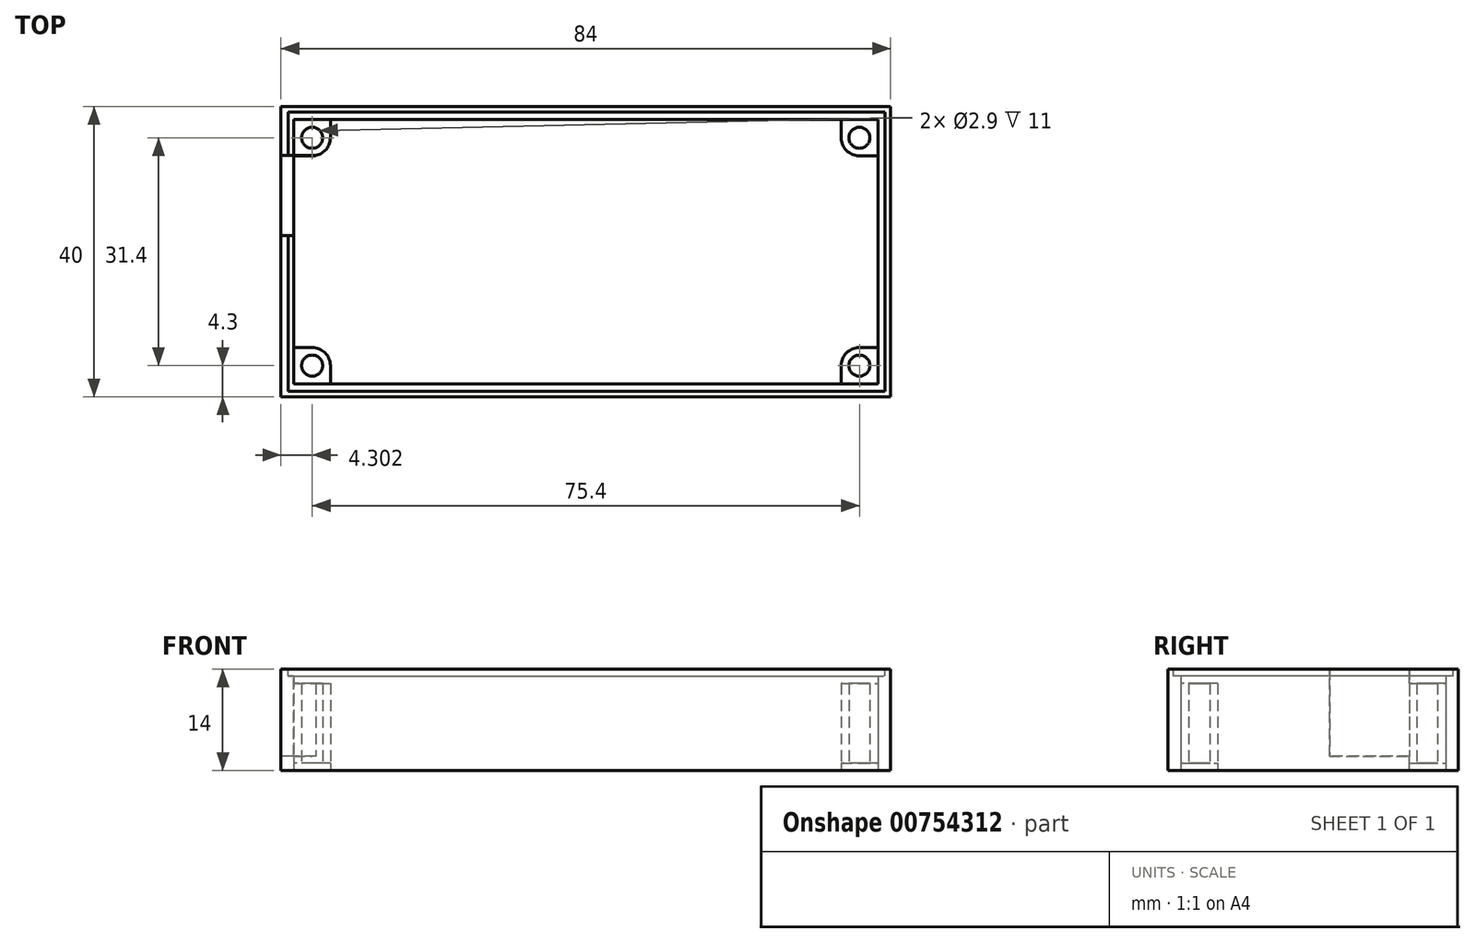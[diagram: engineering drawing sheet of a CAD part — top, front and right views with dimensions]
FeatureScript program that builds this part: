
annotation { "Feature Type Name" : "Feature", "Feature Type Description" : "" }
export const myFeature = defineFeature(function(context is Context, id is Id, definition is map)
    precondition{}
    {
        {
            var Q0;
            Q0=qCreatedBy(makeId("Top.planeOp"),FACE);
            var sketch = newSketch(context, id + "F0", { "sketchPlane" : qUnion([Q0])});
            skLineSegment(sketch, "E0.bottom", {"start": v(-40.69, 13.07) * mm, "end": v(39.81, 13.07) * mm});
            skLineSegment(sketch, "E0.top", {"start": v(-40.69, -23.43) * mm, "end": v(39.81, -23.43) * mm});
            skLineSegment(sketch, "E0.left", {"start": v(-40.69, 13.07) * mm, "end": v(-40.69, -23.43) * mm});
            skLineSegment(sketch, "E0.right", {"start": v(39.81, 13.07) * mm, "end": v(39.81, -23.43) * mm});
            skCircle(sketch, "E1", {"center": v(-38.14, 10.52) * mm, "radius": 1.45 * mm});
            skLineSegment(sketch, "E2", {"start": v(-0.44, 13.07) * mm, "end": v(-0.44, -23.43) * mm, "construction": true});
            skLineSegment(sketch, "E3", {"start": v(-40.69, -5.18) * mm, "end": v(39.81, -5.18) * mm, "construction": true});
            skLineSegment(sketch, "E4.bottom", {"start": v(-42.44, 14.82) * mm, "end": v(41.56, 14.82) * mm});
            skLineSegment(sketch, "E4.top", {"start": v(-42.44, -25.18) * mm, "end": v(41.56, -25.18) * mm});
            skLineSegment(sketch, "E4.left", {"start": v(-42.44, 14.82) * mm, "end": v(-42.44, -25.18) * mm});
            skLineSegment(sketch, "E4.right", {"start": v(41.56, 14.82) * mm, "end": v(41.56, -25.18) * mm});
            skArc(sketch, "E5", {"start": v(-35.64, 10.52) * mm, "mid": v(-36.37, 8.75) * mm, "end": v(-38.14, 8.02) * mm});
            skLineSegment(sketch, "E6", {"start": v(-35.64, 10.52) * mm, "end": v(-35.64, 13.07) * mm});
            skLineSegment(sketch, "E7", {"start": v(-38.14, 8.02) * mm, "end": v(-40.69, 8.02) * mm});
            skCircle(sketch, "E8.MirrorC", {"center": v(37.26, 10.52) * mm, "radius": 1.45 * mm});
            skLineSegment(sketch, "E9.MirrorCS", {"start": v(34.76, 10.52) * mm, "end": v(34.76, 13.07) * mm});
            skLineSegment(sketch, "E10.MirrorCS", {"start": v(37.26, 8.02) * mm, "end": v(39.81, 8.02) * mm});
            skArc(sketch, "E11.MirrorCS", {"start": v(34.76, 10.52) * mm, "mid": v(35.5, 8.75) * mm, "end": v(37.26, 8.02) * mm});
            skCircle(sketch, "E12.MirrorC", {"center": v(37.26, -20.88) * mm, "radius": 1.45 * mm});
            skLineSegment(sketch, "E13.MirrorCS", {"start": v(37.26, -18.38) * mm, "end": v(39.81, -18.38) * mm});
            skArc(sketch, "E14.MirrorCS", {"start": v(34.76, -20.88) * mm, "mid": v(35.5, -19.11) * mm, "end": v(37.26, -18.38) * mm});
            skLineSegment(sketch, "E15.MirrorCS", {"start": v(34.76, -20.88) * mm, "end": v(34.76, -23.43) * mm});
            skCircle(sketch, "E16.MirrorC", {"center": v(-38.14, -20.88) * mm, "radius": 1.45 * mm});
            skLineSegment(sketch, "E17.MirrorCS", {"start": v(-35.64, -20.88) * mm, "end": v(-35.64, -23.43) * mm});
            skLineSegment(sketch, "E18.MirrorCS", {"start": v(-38.14, -18.38) * mm, "end": v(-40.69, -18.38) * mm});
            skArc(sketch, "E19.MirrorCS", {"start": v(-35.64, -20.88) * mm, "mid": v(-36.37, -19.11) * mm, "end": v(-38.14, -18.38) * mm});
            skPoint(sketch, "E20.0.midPoint", {"position": v(39.73, 9.1) * mm});
            skPoint(sketch, "E21.0.midPoint", {"position": v(39.73, -22.3) * mm});
            skPoint(sketch, "E22.0.midPoint", {"position": v(-35.67, -22.3) * mm});
            skPoint(sketch, "E23.0.midPoint", {"position": v(-35.67, 9.1) * mm});
            skSolve(sketch);
        }
        {
            var Q0;
            Q0=makeQuery(id+"F0.imprint","IMPRINT",FACE,{"disambiguationData":[TD([[makeQuery(id+"F0.imprint","IMPRINT",EDGE,{"derivedFrom":sQuery(id+"F0.wireOp",EDGE,"E8.MirrorC")}),-1.0]])]});
            var Q1;
            Q1=makeQuery(id+"F0.imprint","IMPRINT",FACE,{"disambiguationData":[TD([[makeQuery(id+"F0.imprint","IMPRINT",EDGE,{"derivedFrom":sQuery(id+"F0.wireOp",EDGE,"E5")}),1.0]])]});
            var Q2;
            Q2=makeQuery(id+"F0.imprint","IMPRINT",FACE,{"disambiguationData":[TD([[makeQuery(id+"F0.imprint","IMPRINT",EDGE,{"derivedFrom":sQuery(id+"F0.wireOp",EDGE,"E4.bottom")}),-1.0]])]});
            var Q3;
            Q3=makeQuery(id+"F0.imprint","IMPRINT",FACE,{"disambiguationData":[TD([[makeQuery(id+"F0.imprint","IMPRINT",EDGE,{"derivedFrom":sQuery(id+"F0.wireOp",EDGE,"E12.MirrorC")}),-1.0]])]});
            var Q4;
            Q4=makeQuery(id+"F0.imprint","IMPRINT",FACE,{"disambiguationData":[TD([[makeQuery(id+"F0.imprint","IMPRINT",EDGE,{"derivedFrom":sQuery(id+"F0.wireOp",EDGE,"E8.MirrorC")}),1.0]])]});
            var Q5;
            Q5=makeQuery(id+"F0.imprint","IMPRINT",FACE,{"disambiguationData":[TD([[makeQuery(id+"F0.imprint","IMPRINT",EDGE,{"derivedFrom":sQuery(id+"F0.wireOp",EDGE,"E1")}),1.0]])]});
            var Q6;
            Q6=makeQuery(id+"F0.imprint","IMPRINT",FACE,{"disambiguationData":[TD([[makeQuery(id+"F0.imprint","IMPRINT",EDGE,{"derivedFrom":sQuery(id+"F0.wireOp",EDGE,"E12.MirrorC")}),1.0]])]});
            var Q7;
            Q7=makeQuery(id+"F0.imprint","IMPRINT",FACE,{"disambiguationData":[TD([[makeQuery(id+"F0.imprint","IMPRINT",EDGE,{"derivedFrom":sQuery(id+"F0.wireOp",EDGE,"E16.MirrorC")}),-1.0]])]});
            var Q8;
            Q8=makeQuery(id+"F0.imprint","IMPRINT",FACE,{"disambiguationData":[TD([[makeQuery(id+"F0.imprint","IMPRINT",EDGE,{"derivedFrom":sQuery(id+"F0.wireOp",EDGE,"E16.MirrorC")}),1.0]])]});
            var Q9;
            Q9=makeQuery(id+"F0.imprint","IMPRINT",FACE,{"disambiguationData":[TD([[makeQuery(id+"F0.imprint","IMPRINT",EDGE,{"derivedFrom":sQuery(id+"F0.wireOp",EDGE,"E1")}),-1.0]])]});
            extrude(context, id + "F1", {"entities" : qUnion([Q0, Q1, Q2, Q3, Q4, Q5, Q6, Q7, Q8, Q9]), "depth" : 1 * mm, "offsetDistance" : 25 * mm});
        }
        {
            var Q0;
            Q0=makeQuery(id+"F0.imprint","IMPRINT",FACE,{"disambiguationData":[TD([[makeQuery(id+"F0.imprint","IMPRINT",EDGE,{"derivedFrom":sQuery(id+"F0.wireOp",EDGE,"E1")}),-1.0]])]});
            var Q1;
            Q1=makeQuery(id+"F0.imprint","IMPRINT",FACE,{"disambiguationData":[TD([[makeQuery(id+"F0.imprint","IMPRINT",EDGE,{"derivedFrom":sQuery(id+"F0.wireOp",EDGE,"E8.MirrorC")}),1.0]])]});
            var Q2;
            Q2=makeQuery(id+"F0.imprint","IMPRINT",FACE,{"disambiguationData":[TD([[makeQuery(id+"F0.imprint","IMPRINT",EDGE,{"derivedFrom":sQuery(id+"F0.wireOp",EDGE,"E12.MirrorC")}),-1.0]])]});
            var Q3;
            Q3=makeQuery(id+"F0.imprint","IMPRINT",FACE,{"disambiguationData":[TD([[makeQuery(id+"F0.imprint","IMPRINT",EDGE,{"derivedFrom":sQuery(id+"F0.wireOp",EDGE,"E16.MirrorC")}),1.0]])]});
            extrude(context, id + "F2", {"entities" : qUnion([Q0, Q1, Q2, Q3]), "operationType" : NewBodyOperationType.ADD, "depth" : 12 * mm, "offsetDistance" : 25 * mm});
        }
        {
            var Q0;
            Q0=makeQuery(id+"F0.imprint","IMPRINT",FACE,{"disambiguationData":[TD([[makeQuery(id+"F0.imprint","IMPRINT",EDGE,{"derivedFrom":sQuery(id+"F0.wireOp",EDGE,"E4.bottom")}),-1.0]])]});
            extrude(context, id + "F3", {"entities" : qUnion([Q0]), "operationType" : NewBodyOperationType.ADD, "depth" : 14 * mm, "offsetDistance" : 25 * mm});
        }
        {
            var Q0;
            {var subQ0=sQuery(id+"F0.wireOp",EDGE,"E4.left");Q0=makeQuery(id+"F3.boolean.opBoolean","MERGE",FACE,{"derivedFrom":[makeQuery(id+"F1.opExtrude","SWEPT_FACE",FACE,{"disambiguationData":[OSD([subQ0])]}),makeQuery(id+"F3.opExtrude","SWEPT_FACE",FACE,{"disambiguationData":[OSD([subQ0])]})]});}
            var sketch = newSketch(context, id + "F4", { "sketchPlane" : qUnion([Q0])});
            skLineSegment(sketch, "E24.bottom", {"start": v(-8.07, 54.11) * mm, "end": v(2.93, 54.11) * mm});
            skLineSegment(sketch, "E24.top", {"start": v(-8.07, 2) * mm, "end": v(2.93, 2) * mm});
            skLineSegment(sketch, "E24.left", {"start": v(-8.07, 54.11) * mm, "end": v(-8.07, 2) * mm});
            skLineSegment(sketch, "E24.right", {"start": v(2.93, 54.11) * mm, "end": v(2.93, 2) * mm});
            skSolve(sketch);
        }
        {
            var Q0;
            {var subQ0=sQuery(id+"F4.wireOp",EDGE,"E24.top");Q0=makeQuery(id+"F4.imprint","IMPRINT",FACE,{"disambiguationData":[TD([[makeQuery(id+"F4.imprint","IMPRINT",EDGE,{"derivedFrom":subQ0}),1.0]])]});}
            extrude(context, id + "F5", {"entities" : qUnion([Q0]), "operationType" : NewBodyOperationType.REMOVE, "oppositeDirection" : true, "depth" : 25 * mm, "offsetDistance" : 25 * mm});
        }
        {
            var Q0;
            Q0=makeQuery(id+"F3.opExtrude","CAP_FACE",FACE,{"disambiguationData":[OSD([sQuery(id+"F0.wireOp",EDGE,"E0.bottom"),sQuery(id+"F0.wireOp",EDGE,"E0.top"),sQuery(id+"F0.wireOp",EDGE,"E0.left"),sQuery(id+"F0.wireOp",EDGE,"E0.right"),sQuery(id+"F0.wireOp",EDGE,"E4.bottom"),sQuery(id+"F0.wireOp",EDGE,"E4.top"),sQuery(id+"F0.wireOp",EDGE,"E4.left"),sQuery(id+"F0.wireOp",EDGE,"E4.right")])],"isStart":false});
            var sketch = newSketch(context, id + "F6", { "sketchPlane" : qUnion([Q0])});
            skLineSegment(sketch, "E25.bottom", {"start": v(-41.44, 14.07) * mm, "end": v(40.81, 14.07) * mm});
            skLineSegment(sketch, "E25.top", {"start": v(-41.44, -24.43) * mm, "end": v(40.81, -24.43) * mm});
            skLineSegment(sketch, "E25.left", {"start": v(-41.44, 14.07) * mm, "end": v(-41.44, -24.43) * mm});
            skLineSegment(sketch, "E25.right", {"start": v(40.81, 14.07) * mm, "end": v(40.81, -24.43) * mm});
            skSolve(sketch);
        }
        {
            var Q0;
            {var subQ3=sQuery(id+"F6.wireOp",EDGE,"E25.bottom");Q0=makeQuery(id+"F6.imprint","IMPRINT",FACE,{"disambiguationData":[TD([[makeQuery(id+"F6.imprint","IMPRINT",EDGE,{"derivedFrom":subQ3}),-1.0]])]});}
            extrude(context, id + "F7", {"entities" : qUnion([Q0]), "operationType" : NewBodyOperationType.REMOVE, "oppositeDirection" : true, "depth" : 1 * mm, "offsetDistance" : 25 * mm});
        }
    });
